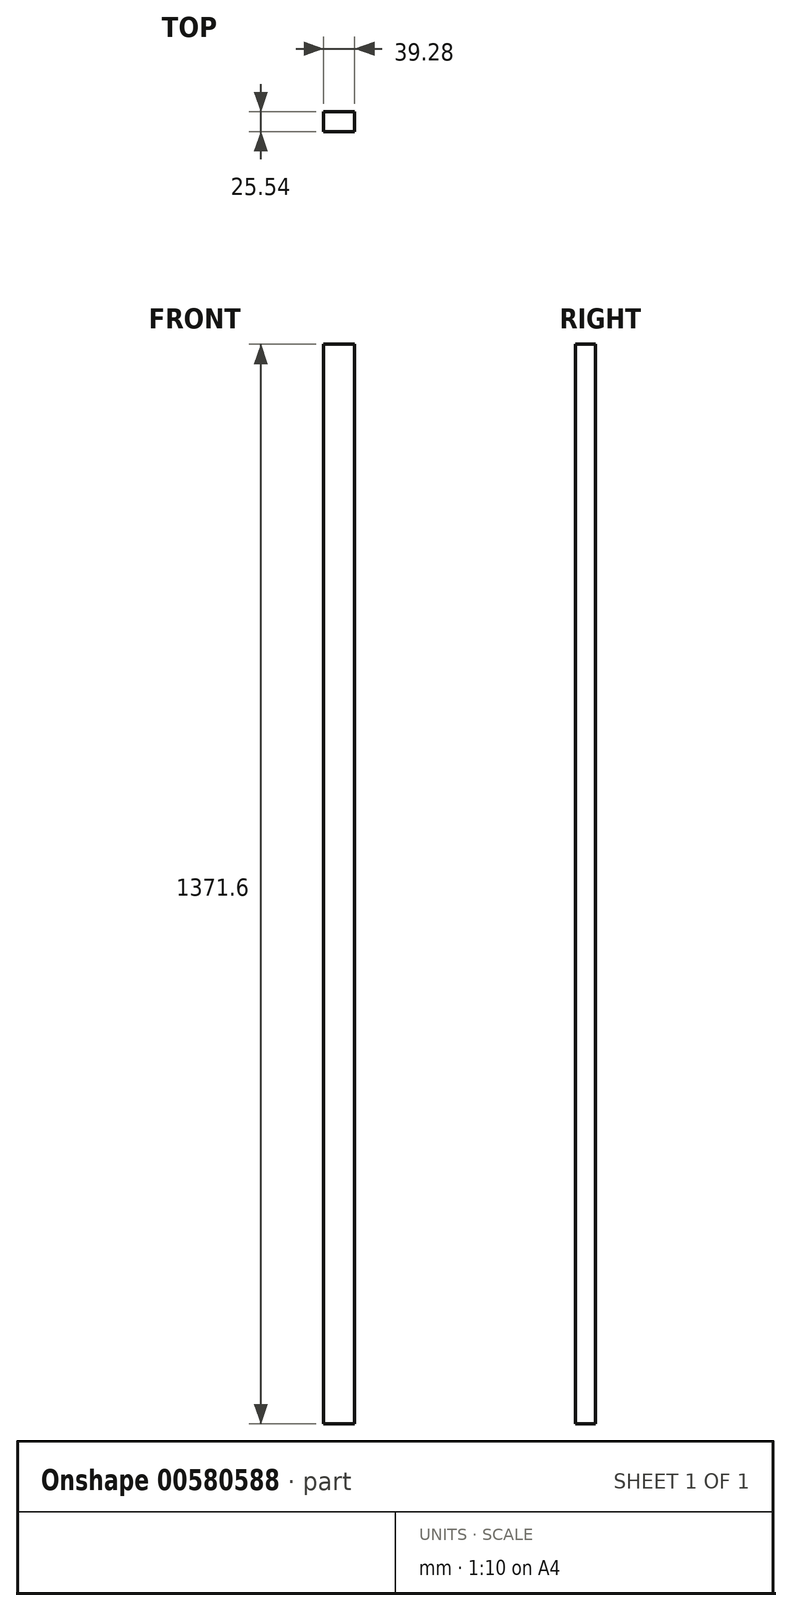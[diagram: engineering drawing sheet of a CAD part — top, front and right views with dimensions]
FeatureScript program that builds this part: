
annotation { "Feature Type Name" : "Feature", "Feature Type Description" : "" }
export const myFeature = defineFeature(function(context is Context, id is Id, definition is map)
    precondition{}
    {
        {
            var Q0;
            Q0=qCreatedBy(makeId("Top.planeOp"),FACE);
            var sketch = newSketch(context, id + "F0", { "sketchPlane" : qUnion([Q0])});
            skLineSegment(sketch, "E0.bottom", {"start": v(19.64, -12.77) * mm, "end": v(-19.64, -12.77) * mm});
            skLineSegment(sketch, "E0.top", {"start": v(19.64, 12.77) * mm, "end": v(-19.64, 12.77) * mm});
            skLineSegment(sketch, "E0.left", {"start": v(19.64, -12.77) * mm, "end": v(19.64, 12.77) * mm});
            skLineSegment(sketch, "E0.right", {"start": v(-19.64, -12.77) * mm, "end": v(-19.64, 12.77) * mm});
            skPoint(sketch, "E0.middle", {"position": v(0, 0) * mm});
            skSolve(sketch);
        }
        {
            var Q0;
            Q0=sQuery(id+"F0.wireOp",EDGE,"E0.right");
            var Q1;
            Q1=sQuery(id+"F0.wireOp",EDGE,"E0.bottom");
            var Q2;
            Q2=sQuery(id+"F0.wireOp",EDGE,"E0.top");
            var Q3;
            Q3=sQuery(id+"F0.wireOp",EDGE,"E0.left");
            extrude(context, id + "F1", {"bodyType" : ToolBodyType.SURFACE, "surfaceEntities" : qUnion([Q0, Q1, Q2, Q3]), "depth" : 1371.6 * mm, "offsetDistance" : 25.4 * mm});
        }
    });
